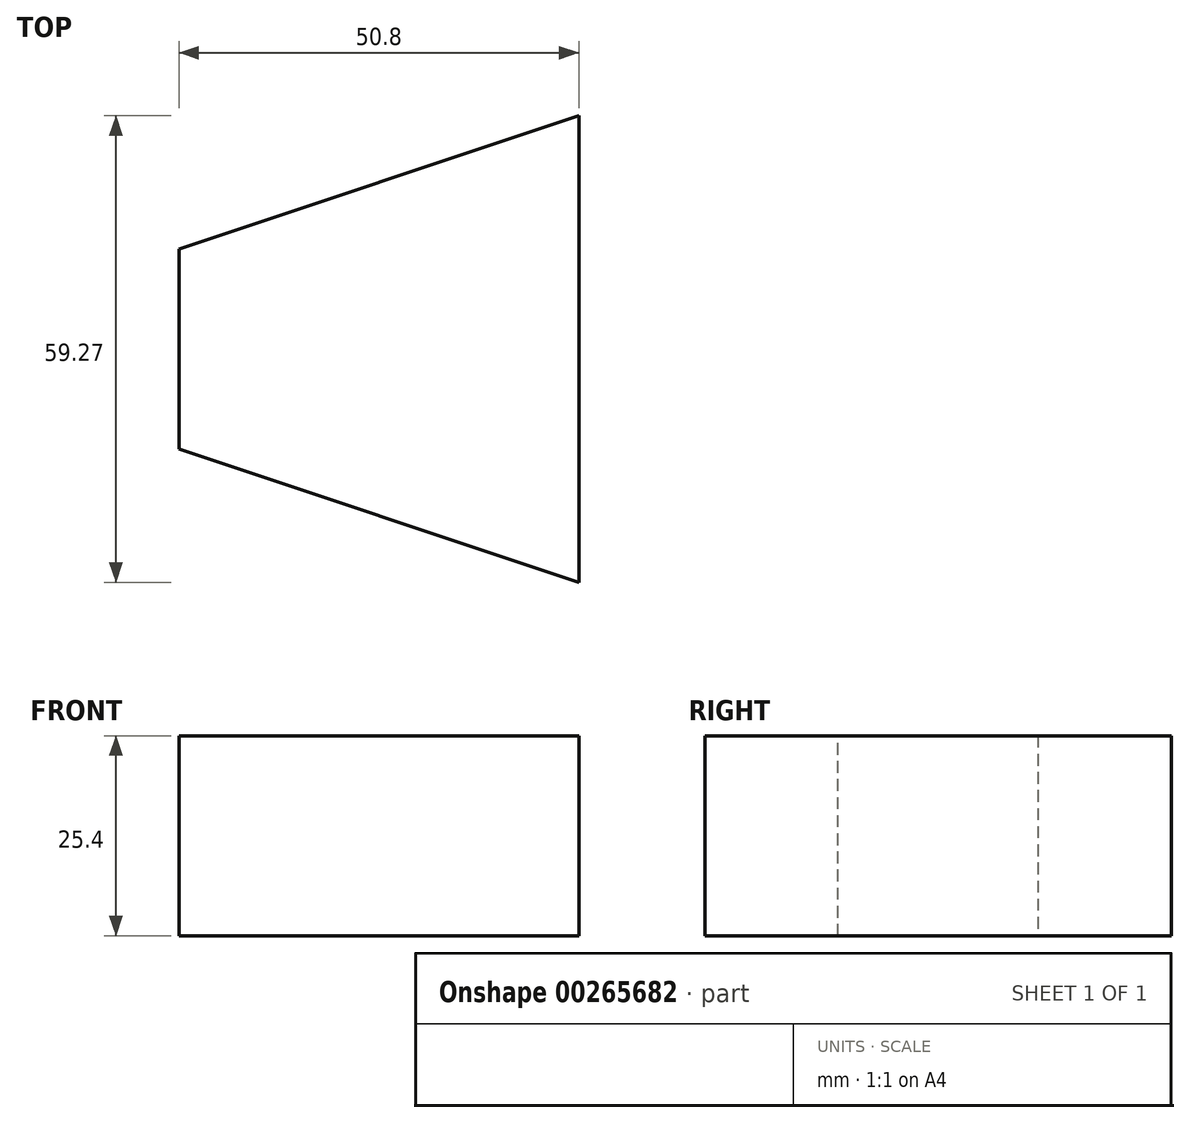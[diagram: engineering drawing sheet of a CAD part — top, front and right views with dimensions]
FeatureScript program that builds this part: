
annotation { "Feature Type Name" : "Feature", "Feature Type Description" : "" }
export const myFeature = defineFeature(function(context is Context, id is Id, definition is map)
    precondition{}
    {
        {
            var Q0;
            Q0=qCreatedBy(makeId("Right.planeOp"),FACE);
            var sketch = newSketch(context, id + "F0", { "sketchPlane" : qUnion([Q0])});
            skLineSegment(sketch, "E0.bottom", {"start": v(-33.06, 25.02) * mm, "end": v(43.14, 25.02) * mm});
            skLineSegment(sketch, "E0.top", {"start": v(-33.06, -0.38) * mm, "end": v(43.14, -0.38) * mm});
            skLineSegment(sketch, "E0.left", {"start": v(-33.06, 25.02) * mm, "end": v(-33.06, -0.38) * mm});
            skLineSegment(sketch, "E0.right", {"start": v(43.14, 25.02) * mm, "end": v(43.14, -0.38) * mm});
            skSolve(sketch);
        }
        {
            var Q0;
            Q0=makeQuery(id+"F0.imprint","IMPRINT",FACE,{"disambiguationData":[TD([[makeQuery(id+"F0.imprint","IMPRINT",EDGE,{"derivedFrom":sQuery(id+"F0.wireOp",EDGE,"E0.bottom")}),-1.0]])]});
            extrude(context, id + "F1", {"entities" : qUnion([Q0]), "depth" : 50.8 * mm});
        }
        {
            var Q0;
            Q0=makeQuery(id+"F1.opExtrude","CAP_EDGE",EDGE,{"disambiguationData":[OSD([sQuery(id+"F0.wireOp",EDGE,"E0.left")])],"isStart":true});
            var Q1;
            Q1=makeQuery(id+"F1.opExtrude","CAP_EDGE",EDGE,{"disambiguationData":[OSD([sQuery(id+"F0.wireOp",EDGE,"E0.right")])],"isStart":true});
            chamfer(context, id + "F2", {"entities" : qUnion([Q0, Q1]), "chamferType" : ChamferType.TWO_OFFSETS, "width1" : 76.2 * mm, "oppositeDirection" : false, "width2" : 25.4 * mm, "tangentPropagation" : true});
        }
    });
